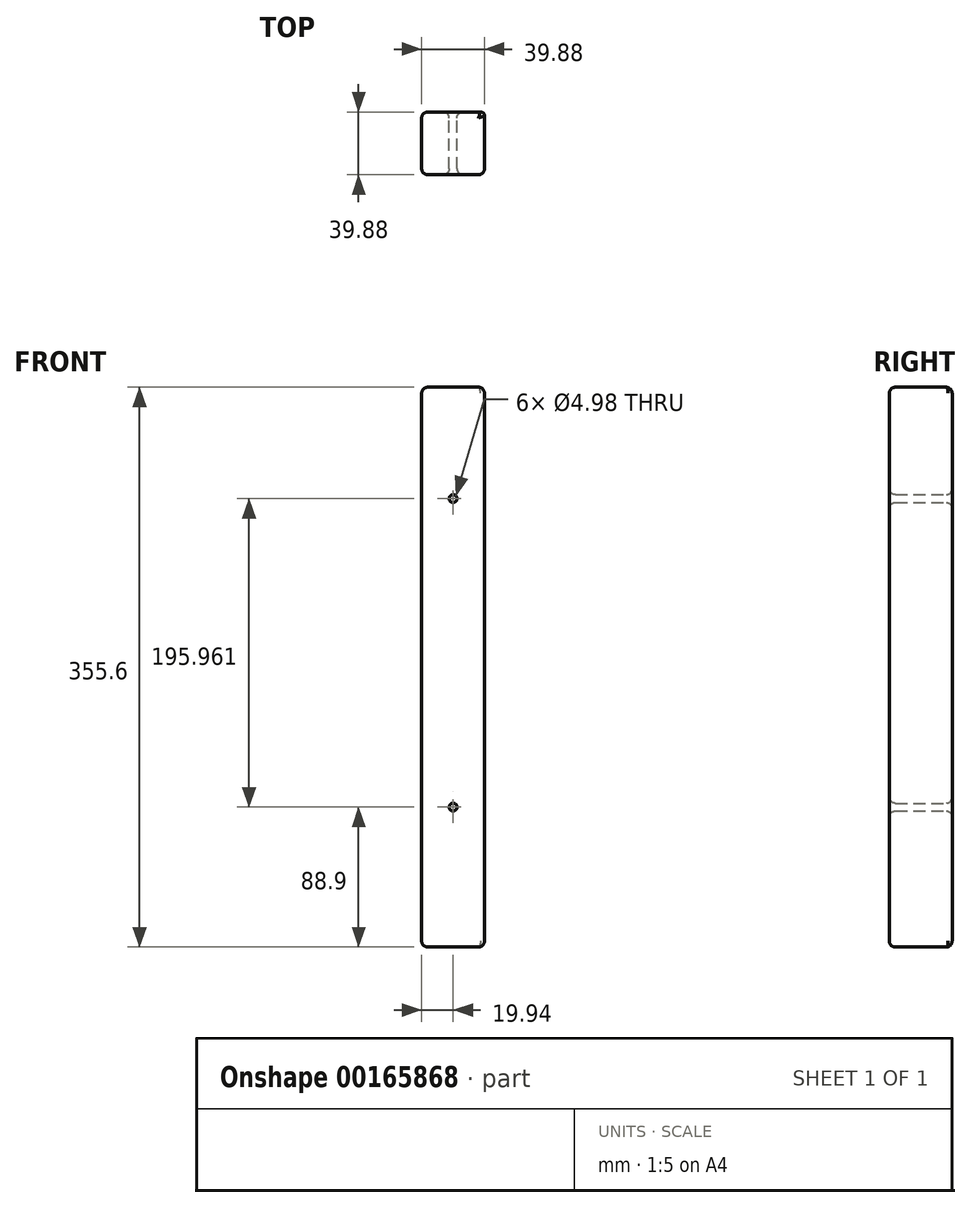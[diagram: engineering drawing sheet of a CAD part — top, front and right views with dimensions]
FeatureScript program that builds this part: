
annotation { "Feature Type Name" : "Feature", "Feature Type Description" : "" }
export const myFeature = defineFeature(function(context is Context, id is Id, definition is map)
    precondition{}
    {
        {
            var Q0;
            Q0=qCreatedBy(makeId("Front.planeOp"),FACE);
            var sketch = newSketch(context, id + "F0", { "sketchPlane" : qUnion([Q0])});
            skLineSegment(sketch, "E0.bottom", {"start": v(19.94, -177.8) * mm, "end": v(-19.94, -177.8) * mm});
            skLineSegment(sketch, "E0.top", {"start": v(19.94, 177.8) * mm, "end": v(-19.94, 177.8) * mm});
            skLineSegment(sketch, "E0.left", {"start": v(19.94, -177.8) * mm, "end": v(19.94, 177.8) * mm});
            skLineSegment(sketch, "E0.right", {"start": v(-19.94, -177.8) * mm, "end": v(-19.94, 177.8) * mm});
            skPoint(sketch, "E0.middle", {"position": v(0, 0) * mm});
            skCircle(sketch, "E1", {"center": v(0, 107.06) * mm, "radius": 2.49 * mm});
            skLineSegment(sketch, "E2", {"start": v(-19.94, -177.8) * mm, "end": v(-19.94, -101.6) * mm});
            skLineSegment(sketch, "E3", {"start": v(-19.94, -101.6) * mm, "end": v(19.94, -101.6) * mm});
            skCircle(sketch, "E4", {"center": v(0, -88.9) * mm, "radius": 2.49 * mm});
            skSolve(sketch);
        }
        {
            var Q0;
            Q0 = qSketchRegion(id + "F0", true);
            extrude(context, id + "F1", {"entities" : qUnion([Q0]), "depth" : 39.88 * mm});
        }
        {
            var Q0;
            Q0=makeQuery(id+"F1.opExtrude","CAP_EDGE",EDGE,{"disambiguationData":[OSD([sQuery(id+"F0.wireOp",EDGE,"E0.right"),sQuery(id+"F0.wireOp",EDGE,"E2")])],"isStart":false});
            var Q1;
            Q1=makeQuery(id+"F1.opExtrude","CAP_EDGE",EDGE,{"disambiguationData":[OSD([sQuery(id+"F0.wireOp",EDGE,"E0.right"),sQuery(id+"F0.wireOp",EDGE,"E2")])],"isStart":true});
            var Q2;
            Q2=makeQuery(id+"F1.opExtrude","CAP_EDGE",EDGE,{"disambiguationData":[OSD([sQuery(id+"F0.wireOp",EDGE,"E1")])],"isStart":true});
            var Q3;
            Q3=makeQuery(id+"F1.opExtrude","CAP_EDGE",EDGE,{"disambiguationData":[OSD([sQuery(id+"F0.wireOp",EDGE,"E4")])],"isStart":true});
            var Q4;
            Q4=makeQuery(id+"F1.opExtrude","CAP_EDGE",EDGE,{"disambiguationData":[OSD([sQuery(id+"F0.wireOp",EDGE,"E4")])],"isStart":false});
            var Q5;
            Q5=makeQuery(id+"F1.opExtrude","CAP_EDGE",EDGE,{"disambiguationData":[OSD([sQuery(id+"F0.wireOp",EDGE,"E0.left")])],"isStart":false});
            var Q6;
            Q6=makeQuery(id+"F1.opExtrude","CAP_EDGE",EDGE,{"disambiguationData":[OSD([sQuery(id+"F0.wireOp",EDGE,"E1")])],"isStart":false});
            fillet(context, id + "F2", {"entities" : qUnion([Q0, Q1, Q2, Q3, Q4, Q5, Q6]), "radius" : 3.8 * mm, "tangentPropagation" : true, "allowEdgeOverflow" : false});
        }
        {
            var Q0;
            Q0=makeQuery(id+"F1.opExtrude","CAP_EDGE",EDGE,{"disambiguationData":[OSD([sQuery(id+"F0.wireOp",EDGE,"E0.top")])],"isStart":false});
            var Q1;
            Q1=makeQuery(id+"F1.opExtrude","SWEPT_EDGE",EDGE,{"disambiguationData":[OSD([sQuery(id+"F0.wireOp",EDGE,"E0.top"),sQuery(id+"F0.wireOp",EDGE,"E0.left")])]});
            var Q2;
            Q2=makeQuery(id+"F1.opExtrude","CAP_EDGE",EDGE,{"disambiguationData":[OSD([sQuery(id+"F0.wireOp",EDGE,"E0.top")])],"isStart":true});
            var Q3;
            Q3=makeQuery(id+"F1.opExtrude","SWEPT_EDGE",EDGE,{"disambiguationData":[OSD([sQuery(id+"F0.wireOp",EDGE,"E0.top"),sQuery(id+"F0.wireOp",EDGE,"E0.right")])]});
            var Q4;
            Q4=makeQuery(id+"F1.opExtrude","CAP_EDGE",EDGE,{"disambiguationData":[OSD([sQuery(id+"F0.wireOp",EDGE,"E0.bottom")])],"isStart":false});
            var Q5;
            Q5=makeQuery(id+"F1.opExtrude","SWEPT_EDGE",EDGE,{"disambiguationData":[OSD([sQuery(id+"F0.wireOp",EDGE,"E0.bottom"),sQuery(id+"F0.wireOp",EDGE,"E2")])]});
            var Q6;
            Q6=makeQuery(id+"F1.opExtrude","CAP_EDGE",EDGE,{"disambiguationData":[OSD([sQuery(id+"F0.wireOp",EDGE,"E0.bottom")])],"isStart":true});
            var Q7;
            Q7=makeQuery(id+"F1.opExtrude","SWEPT_EDGE",EDGE,{"disambiguationData":[OSD([sQuery(id+"F0.wireOp",EDGE,"E0.bottom"),sQuery(id+"F0.wireOp",EDGE,"E0.left")])]});
            fillet(context, id + "F3", {"entities" : qUnion([Q0, Q1, Q2, Q3, Q4, Q5, Q6, Q7]), "radius" : 3.8 * mm, "tangentPropagation" : true, "allowEdgeOverflow" : false});
        }
        {
            var Q0;
            Q0=makeQuery(id+"F1.opExtrude","CAP_EDGE",EDGE,{"disambiguationData":[OSD([sQuery(id+"F0.wireOp",EDGE,"E0.left")])],"isStart":true});
            fillet(context, id + "F4", {"entities" : qUnion([Q0]), "radius" : 2.54 * mm, "tangentPropagation" : true, "allowEdgeOverflow" : false});
        }
    });
